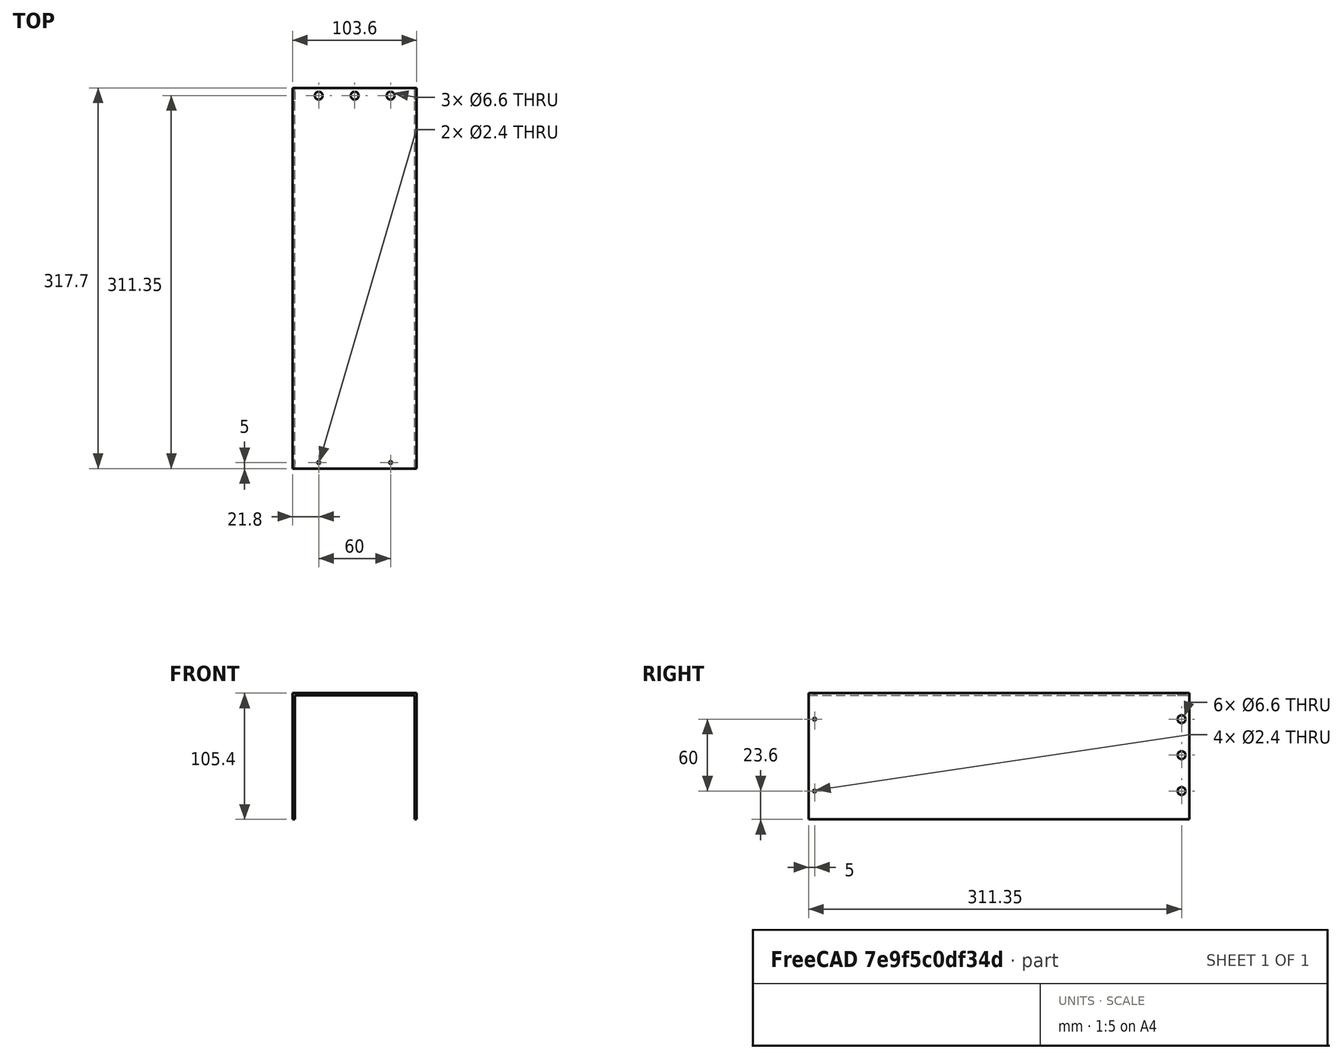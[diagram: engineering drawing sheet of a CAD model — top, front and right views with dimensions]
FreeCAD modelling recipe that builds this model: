
FCSTD DOCUMENT  (FreeCAD 0.20R29603 (Git))
Label: MechanicalCF35Mount003
License: All rights reserved
LicenseURL: http://en.wikipedia.org/wiki/All_rights_reserved
objects: Part::Cylinder×14, TechDraw::DrawViewDimension×13, Part::Compound×10, TechDraw::DrawProjGroupItem×4, Part::Box×3, Part::Cut×2, Part::FeaturePython×1, Part::Feature×1, TechDraw::DrawSVGTemplate×1, TechDraw::DrawProjGroup×1, TechDraw::DrawPage×1
note: 31 computed .brp shape members not serialized (recipe doc carries the construction recipe); baked Part::Feature solids carry a one-line shape summary decoded from their .brp

FEATURE [Part::Box] Box  label="Würfel"
  AttacherType = Attacher::AttachEngine3D
  Height = 1.8
  Length = 103.6
  Placement = pos=(-51.8,-305,50) rot=(0,0,1;0rad)
  Width = 317.7
FEATURE [Part::Box] Box001  label="Würfel001"
  AttacherType = Attacher::AttachEngine3D
  Height = 1.8
  Length = 103.6
  Placement = pos=(-51.8,-305,50) rot=(0,1,0;1.5708rad)
  Width = 317.7
FEATURE [Part::Box] Box002  label="Würfel002"
  AttacherType = Attacher::AttachEngine3D
  Height = 1.8
  Length = 103.6
  Placement = pos=(50,-305,50) rot=(0,1,0;1.5708rad)
  Width = 317.7
FEATURE [Part::Compound] Compound006
  Links = -> [Box,Box001,Box002]
FEATURE [Part::Cylinder] Cylinder004  label="Zylinder004"
  Angle = 360
  AttacherType = Attacher::AttachEngine3D
  FirstAngle = 0
  Height = 200
  Placement = pos=(30,6.35,-100) rot=(0,0,1;0rad)
  Radius = 3.3
  SecondAngle = 0
FEATURE [Part::Cylinder] Cylinder005  label="Zylinder005"
  Angle = 360
  AttacherType = Attacher::AttachEngine3D
  FirstAngle = 0
  Height = 200
  Placement = pos=(-30,6.35,-100) rot=(0,0,1;0rad)
  Radius = 3.3
  SecondAngle = 0
FEATURE [Part::Cylinder] Cylinder006  label="Zylinder006"
  Angle = 360
  AttacherType = Attacher::AttachEngine3D
  FirstAngle = 0
  Height = 200
  Placement = pos=(-30,6.35,-100) rot=(0,0,1;0rad)
  Radius = 3.3
  SecondAngle = 0
FEATURE [Part::Cylinder] Cylinder007  label="Zylinder007"
  Angle = 360
  AttacherType = Attacher::AttachEngine3D
  FirstAngle = 0
  Height = 200
  Placement = pos=(30,6.35,-100) rot=(0,0,1;0rad)
  Radius = 3.3
  SecondAngle = 0
FEATURE [Part::Compound] Compound004
  Links = -> [Cylinder006,Cylinder007]
  Placement = pos=(0,0,0) rot=(0,1,0;1.5708rad)
FEATURE [Part::Compound] Compound005
  Links = -> [Cylinder004,Cylinder005,Compound004]
FEATURE [Part::Cylinder] Cylinder008  label="Zylinder008"
  Angle = 360
  AttacherType = Attacher::AttachEngine3D
  FirstAngle = 0
  Height = 200
  Placement = pos=(0,6.35,-100) rot=(0,0,1;0rad)
  Radius = 3.3
  SecondAngle = 0
FEATURE [Part::Cylinder] Cylinder009  label="Zylinder009"
  Angle = 360
  AttacherType = Attacher::AttachEngine3D
  FirstAngle = 0
  Height = 200
  Placement = pos=(0,6.35,-100) rot=(0,0,1;0rad)
  Radius = 3.3
  SecondAngle = 0
FEATURE [Part::Compound] Compound007
  Links = -> [Cylinder009]
  Placement = pos=(0,0,0) rot=(0,1,0;1.5708rad)
FEATURE [Part::Compound] Compound008
  Links = -> [Compound005,Cylinder008,Compound007]
FEATURE [Part::Cut] Cut
  Base = -> Compound006
  Tool = -> Compound008
FEATURE [Part::FeaturePython] Connect  # WARN: FeaturePython — macro-defined, semantics opaque (R4)
  Objects = -> [Cut]
  Tolerance = 0
FEATURE [Part::Cylinder] Cylinder  label="Zylinder"
  Angle = 360
  AttacherType = Attacher::AttachEngine3D
  FirstAngle = 0
  Height = 20
  Placement = pos=(30,2,40) rot=(0,0,1;0rad)
  Radius = 1.2
  SecondAngle = 0
FEATURE [Part::Cylinder] Cylinder015  label="Zylinder015"
  Angle = 360
  AttacherType = Attacher::AttachEngine3D
  FirstAngle = 0
  Height = 20
  Placement = pos=(-30,2,40) rot=(0,0,1;0rad)
  Radius = 1.2
  SecondAngle = 0
FEATURE [Part::Compound] Compound
  Links = -> [Cylinder,Cylinder015]
FEATURE [Part::Cylinder] Cylinder016  label="Zylinder016"
  Angle = 360
  AttacherType = Attacher::AttachEngine3D
  FirstAngle = 0
  Height = 20
  Placement = pos=(30,2,40) rot=(0,0,1;0rad)
  Radius = 1.2
  SecondAngle = 0
FEATURE [Part::Cylinder] Cylinder017  label="Zylinder017"
  Angle = 360
  AttacherType = Attacher::AttachEngine3D
  FirstAngle = 0
  Height = 20
  Placement = pos=(-30,2,40) rot=(0,0,1;0rad)
  Radius = 1.2
  SecondAngle = 0
FEATURE [Part::Compound] Compound015
  Links = -> [Cylinder016,Cylinder017]
  Placement = pos=(0,0,0) rot=(0,1,0;1.5708rad)
FEATURE [Part::Cylinder] Cylinder018  label="Zylinder018"
  Angle = 360
  AttacherType = Attacher::AttachEngine3D
  FirstAngle = 0
  Height = 20
  Placement = pos=(30,2,40) rot=(0,0,1;0rad)
  Radius = 1.2
  SecondAngle = 0
FEATURE [Part::Cylinder] Cylinder019  label="Zylinder019"
  Angle = 360
  AttacherType = Attacher::AttachEngine3D
  FirstAngle = 0
  Height = 20
  Placement = pos=(-30,2,40) rot=(0,0,1;0rad)
  Radius = 1.2
  SecondAngle = 0
FEATURE [Part::Compound] Compound016
  Links = -> [Cylinder018,Cylinder019]
  Placement = pos=(0,0,0) rot=(0,1,0;3.14159rad)
FEATURE [Part::Cylinder] Cylinder020  label="Zylinder020"
  Angle = 360
  AttacherType = Attacher::AttachEngine3D
  FirstAngle = 0
  Height = 20
  Placement = pos=(30,2,40) rot=(0,0,1;0rad)
  Radius = 1.2
  SecondAngle = 0
FEATURE [Part::Cylinder] Cylinder021  label="Zylinder021"
  Angle = 360
  AttacherType = Attacher::AttachEngine3D
  FirstAngle = 0
  Height = 20
  Placement = pos=(-30,2,40) rot=(0,0,1;0rad)
  Radius = 1.2
  SecondAngle = 0
FEATURE [Part::Compound] Compound017
  Links = -> [Cylinder020,Cylinder021]
  Placement = pos=(0,0,0) rot=(0,-1,0;1.5708rad)
FEATURE [Part::Compound] Compound018  label="M2Corehole"
  Links = -> [Compound017,Compound,Compound015,Compound016]
  Placement = pos=(0,-302,0) rot=(0,0,1;0rad)
FEATURE [Part::Cut] Cut001
  Base = -> Connect
  Tool = -> Compound018
FEATURE [Part::Feature] Cut001_solid  label="Cut001 (Solid)"
  shape: bbox 103.6 x 317.7 x 105.4 mm, 31 faces (baked)
FEATURE [TechDraw::DrawSVGTemplate] Template
  EditableTexts = Designed_by_Name=Thomas Spielauer; FC-Date=2023-07-05; FC-SC=mm; FC-SH=01; FC-Title=CF40 electronics housing; Subtitle=Cover sheet
  Height = 210
  Orientation = 1
  Width = 297
FEATURE [TechDraw::DrawProjGroupItem] ProjItem  label="Front"
  CoarseView = false
  Direction = (0,0,1)
  Focus = 100
  HardHidden = false
  IsoCount = 0
  IsoHidden = false
  IsoVisible = false
  LockPosition = true
  Perspective = false
  Rotation = 0
  RotationVector = (1,0,0)
  Scale = 0.333333
  ScaleType = 2
  SeamHidden = false
  SeamVisible = true
  SmoothHidden = false
  SmoothVisible = true
  Source = -> [Cut001]
  Type = 0
  X = 0
  XDirection = (1,0,0)
  Y = 0
FEATURE [TechDraw::DrawProjGroupItem] ProjItem001  label="Right"
  CoarseView = false
  Direction = (1,0,1e-16)
  Focus = 100
  HardHidden = false
  IsoCount = 0
  IsoHidden = false
  IsoVisible = false
  LockPosition = false
  Perspective = false
  Rotation = 0
  RotationVector = (1,0,0)
  Scale = 0.333333
  ScaleType = 2
  SeamHidden = false
  SeamVisible = true
  SmoothHidden = false
  SmoothVisible = true
  Source = -> [Cut001]
  Type = 2
  X = -35.1333
  XDirection = (1e-16,0,-1)
  Y = 0
FEATURE [TechDraw::DrawProjGroupItem] ProjItem002  label="Left"
  CoarseView = false
  Direction = (-1,0,1e-16)
  Focus = 100
  HardHidden = false
  IsoCount = 0
  IsoHidden = false
  IsoVisible = false
  LockPosition = false
  Perspective = false
  Rotation = 0
  RotationVector = (1,0,0)
  Scale = 0.333333
  ScaleType = 2
  SeamHidden = false
  SeamVisible = true
  SmoothHidden = false
  SmoothVisible = true
  Source = -> [Cut001]
  Type = 1
  X = 35.1333
  XDirection = (1e-16,0,1)
  Y = 0
FEATURE [TechDraw::DrawProjGroupItem] ProjItem003  label="Bottom"
  CoarseView = false
  Direction = (0,-1,0)
  Focus = 100
  HardHidden = false
  IsoCount = 0
  IsoHidden = false
  IsoVisible = false
  LockPosition = false
  Perspective = false
  Rotation = 0
  RotationVector = (1,0,0)
  ScaleType = 2
  SeamHidden = false
  SeamVisible = true
  SmoothHidden = false
  SmoothVisible = true
  Source = -> [Cut001]
  Type = 5
  X = 0
  XDirection = (1,0,0)
  Y = -90.9455
FEATURE [TechDraw::DrawProjGroup] ProjGroup
  Anchor = -> ProjItem
  AutoDistribute = true
  LockPosition = false
  ProjectionType = 0
  Rotation = 0
  Scale = 0.333333
  ScaleType = 2
  Source = -> [Cut001]
  Views = -> [ProjItem,ProjItem001,ProjItem002,ProjItem003]
  X = 86.7905
  Y = 137.808
  spacingX = 0
  spacingY = 0
FEATURE [TechDraw::DrawViewDimension] Dimension
  AngleOverride = false
  Arbitrary = false
  ArbitraryTolerances = false
  EqualTolerance = true
  ExtensionAngle = 0
  FormatSpec = %.2w
  FormatSpecOverTolerance = %+.2w
  FormatSpecUnderTolerance = %+.2w
  Inverted = false
  LineAngle = 0
  LockPosition = false
  MeasureType = 1
  OverTolerance = 0
  References2D = -> [ProjItem003]
  Rotation = 0
  ScaleType = 0
  TheoreticalExact = false
  Type = 0
  UnderTolerance = 0
  X = 21.5083
  Y = -23.6998
FEATURE [TechDraw::DrawViewDimension] Dimension001
  AngleOverride = false
  Arbitrary = false
  ArbitraryTolerances = false
  EqualTolerance = true
  ExtensionAngle = 0
  FormatSpec = %.2w
  FormatSpecOverTolerance = %+.2w
  FormatSpecUnderTolerance = %+.2w
  Inverted = false
  LineAngle = 0
  LockPosition = false
  MeasureType = 1
  OverTolerance = 0
  References2D = -> [ProjItem003]
  Rotation = 0
  ScaleType = 0
  TheoreticalExact = false
  Type = 0
  UnderTolerance = 0
  X = 0.573136
  Y = 27.3701
FEATURE [TechDraw::DrawViewDimension] Dimension002
  AngleOverride = false
  Arbitrary = false
  ArbitraryTolerances = false
  EqualTolerance = true
  ExtensionAngle = 0
  FormatSpec = %.2w
  FormatSpecOverTolerance = %+.2w
  FormatSpecUnderTolerance = %+.2w
  Inverted = false
  LineAngle = 0
  LockPosition = false
  MeasureType = 1
  OverTolerance = 0
  References2D = -> [ProjItem003]
  Rotation = 0
  ScaleType = 0
  TheoreticalExact = false
  Type = 0
  UnderTolerance = 0
  X = -22.7166
  Y = 2.30499
FEATURE [TechDraw::DrawViewDimension] Dimension003
  AngleOverride = false
  Arbitrary = false
  ArbitraryTolerances = false
  EqualTolerance = true
  ExtensionAngle = 0
  FormatSpec = %.2w
  FormatSpecOverTolerance = %+.2w
  FormatSpecUnderTolerance = %+.2w
  Inverted = false
  LineAngle = 0
  LockPosition = false
  MeasureType = 1
  OverTolerance = 0
  References2D = -> [ProjItem002]
  Rotation = 0
  ScaleType = 0
  TheoreticalExact = false
  Type = 0
  UnderTolerance = 0
  X = 31.3231
  Y = 1.75722
FEATURE [TechDraw::DrawViewDimension] Dimension004
  AngleOverride = false
  Arbitrary = false
  ArbitraryTolerances = false
  EqualTolerance = true
  ExtensionAngle = 0
  FormatSpec = %.2w
  FormatSpecOverTolerance = %+.2w
  FormatSpecUnderTolerance = %+.2w
  Inverted = false
  LineAngle = 0
  LockPosition = false
  MeasureType = 1
  OverTolerance = 0
  References2D = -> [ProjItem002]
  Rotation = 0
  ScaleType = 0
  TheoreticalExact = false
  Type = 0
  UnderTolerance = 0
  X = -0.30401
  Y = 61.5395
FEATURE [TechDraw::DrawViewDimension] Dimension005
  AngleOverride = false
  Arbitrary = false
  ArbitraryTolerances = false
  EqualTolerance = true
  ExtensionAngle = 0
  FormatSpec = %.2w
  FormatSpecOverTolerance = %+.2w
  FormatSpecUnderTolerance = %+.2w
  Inverted = false
  LineAngle = 0
  LockPosition = false
  MeasureType = 1
  OverTolerance = 0
  References2D = -> [ProjItem]
  Rotation = 0
  ScaleType = 0
  TheoreticalExact = false
  Type = 0
  UnderTolerance = 0
  X = 0.35821
  Y = 61.5395
FEATURE [TechDraw::DrawViewDimension] Dimension006
  AngleOverride = false
  Arbitrary = false
  ArbitraryTolerances = false
  EqualTolerance = true
  ExtensionAngle = 0
  FormatSpec = %.2w
  FormatSpecOverTolerance = %+.2w
  FormatSpecUnderTolerance = %+.2w
  Inverted = false
  LineAngle = 0
  LockPosition = false
  MeasureType = 1
  OverTolerance = 0
  References2D = -> [ProjItem001]
  Rotation = 0
  ScaleType = 0
  TheoreticalExact = false
  Type = 0
  UnderTolerance = 0
  X = 0.901027
  Y = 61.7783
FEATURE [TechDraw::DrawViewDimension] Dimension007
  AngleOverride = false
  Arbitrary = false
  ArbitraryTolerances = false
  EqualTolerance = true
  ExtensionAngle = 0
  FormatSpec = %.2w
  FormatSpecOverTolerance = %+.2w
  FormatSpecUnderTolerance = %+.2w
  Inverted = false
  LineAngle = 0
  LockPosition = false
  MeasureType = 1
  OverTolerance = 0
  References2D = -> [ProjItem002]
  Rotation = 0
  ScaleType = 0
  TheoreticalExact = false
  Type = 0
  UnderTolerance = 0
  X = 13.1295
  Y = -40.785
FEATURE [TechDraw::DrawViewDimension] Dimension008
  AngleOverride = false
  Arbitrary = false
  ArbitraryTolerances = false
  EqualTolerance = true
  ExtensionAngle = 0
  FormatSpec = %.2w
  FormatSpecOverTolerance = %+.2w
  FormatSpecUnderTolerance = %+.2w
  Inverted = false
  LineAngle = 0
  LockPosition = false
  MeasureType = 1
  OverTolerance = 0
  References2D = -> [ProjItem002]
  Rotation = 0
  ScaleType = 0
  TheoreticalExact = false
  Type = 0
  UnderTolerance = 0
  X = 4.06525
  Y = -54.1819
FEATURE [TechDraw::DrawViewDimension] Dimension009
  AngleOverride = false
  Arbitrary = false
  ArbitraryTolerances = false
  EqualTolerance = true
  ExtensionAngle = 0
  FormatSpec = ⌀%.2w (6x)
  FormatSpecOverTolerance = %+.2w
  FormatSpecUnderTolerance = %+.2w
  Inverted = false
  LineAngle = 0
  LockPosition = false
  MeasureType = 1
  OverTolerance = 0
  References2D = -> [ProjItem]
  Rotation = 0
  ScaleType = 0
  TheoreticalExact = false
  Type = 5
  UnderTolerance = 0
  X = 4.91331
  Y = -37.9481
FEATURE [TechDraw::DrawViewDimension] Dimension010
  AngleOverride = false
  Arbitrary = false
  ArbitraryTolerances = false
  EqualTolerance = true
  ExtensionAngle = 0
  FormatSpec = %.2w
  FormatSpecOverTolerance = %+.2w
  FormatSpecUnderTolerance = %+.2w
  Inverted = false
  LineAngle = 0
  LockPosition = false
  MeasureType = 1
  OverTolerance = 0
  References2D = -> [ProjItem002]
  Rotation = 0
  ScaleType = 0
  TheoreticalExact = false
  Type = 0
  UnderTolerance = 0
  X = 13.3665
  Y = 47.2497
FEATURE [TechDraw::DrawViewDimension] Dimension011
  AngleOverride = false
  Arbitrary = false
  ArbitraryTolerances = false
  EqualTolerance = true
  ExtensionAngle = 0
  FormatSpec = %.2w
  FormatSpecOverTolerance = %+.2w
  FormatSpecUnderTolerance = %+.2w
  Inverted = false
  LineAngle = 0
  LockPosition = false
  MeasureType = 1
  OverTolerance = 0
  References2D = -> [ProjItem002]
  Rotation = 0
  ScaleType = 0
  TheoreticalExact = false
  Type = 0
  UnderTolerance = 0
  X = 13.4962
  Y = 39.3495
FEATURE [TechDraw::DrawViewDimension] Dimension012
  AngleOverride = false
  Arbitrary = false
  ArbitraryTolerances = false
  EqualTolerance = true
  ExtensionAngle = 0
  FormatSpec = ⌀%.2w (9x)
  FormatSpecOverTolerance = %+.2w
  FormatSpecUnderTolerance = %+.2w
  Inverted = false
  LineAngle = 0
  LockPosition = false
  MeasureType = 1
  OverTolerance = 0
  References2D = -> [ProjItem]
  Rotation = 0
  ScaleType = 0
  TheoreticalExact = false
  Type = 5
  UnderTolerance = 0
  X = 6.43535
  Y = 37.659
FEATURE [TechDraw::DrawPage] Page
  KeepUpdated = true
  NextBalloonIndex = 1
  ProjectionType = 0
  Template = -> Template
  Views = -> [ProjGroup,Dimension,Dimension001,Dimension002,Dimension003,Dimension004,Dimension005,Dimension006,Dimension007,Dimension008,Dimension009,Dimension010,Dimension011,Dimension012]
